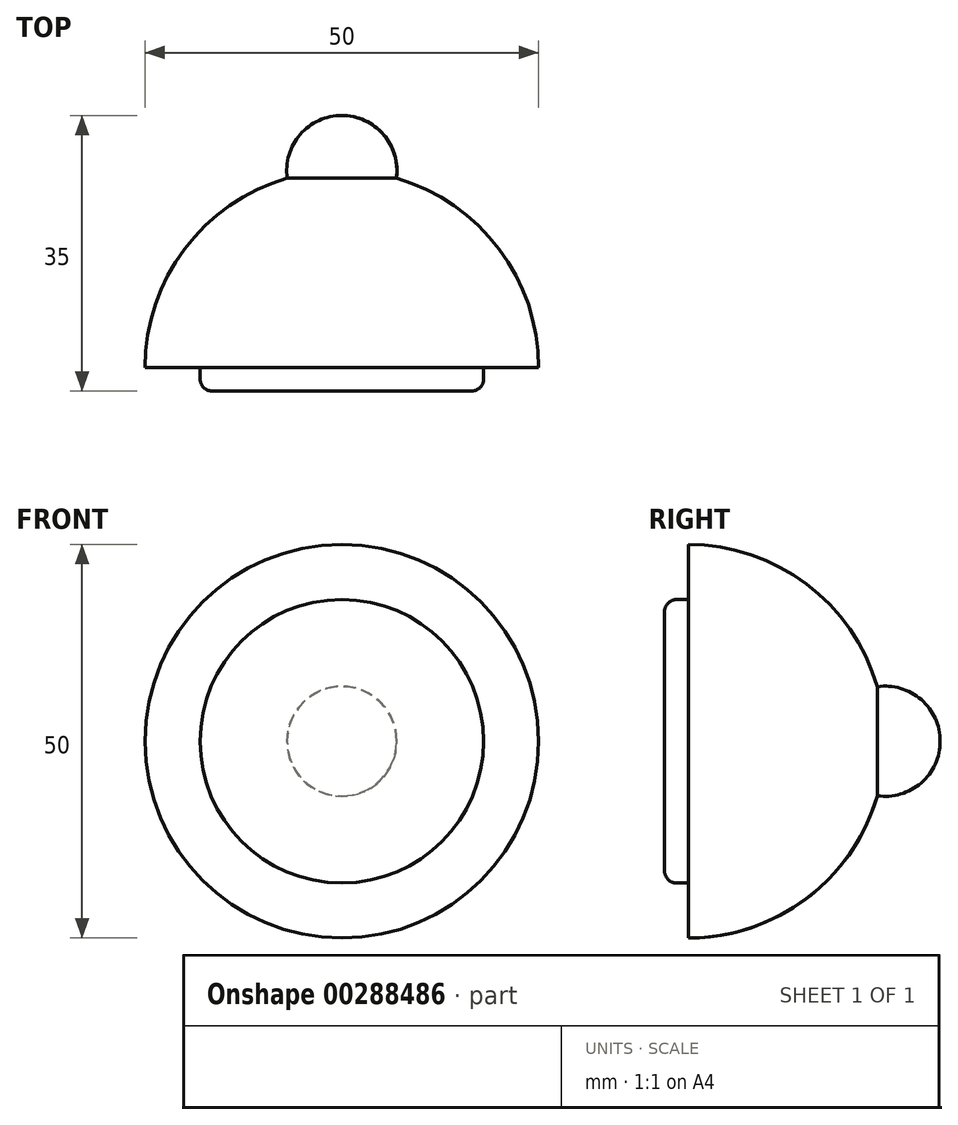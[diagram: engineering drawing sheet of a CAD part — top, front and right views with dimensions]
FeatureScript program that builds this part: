
annotation { "Feature Type Name" : "Feature", "Feature Type Description" : "" }
export const myFeature = defineFeature(function(context is Context, id is Id, definition is map)
    precondition{}
    {
        {
            var Q0;
            Q0=qCreatedBy(makeId("Top.planeOp"),FACE);
            var sketch = newSketch(context, id + "F0", { "sketchPlane" : qUnion([Q0])});
            skPoint(sketch, "E0", {"position": v(0, 25) * mm});
            skPoint(sketch, "E1", {"position": v(25, 0) * mm});
            skArc(sketch, "E2", {"start": v(25, 0) * mm, "mid": v(19.98, 15.03) * mm, "end": v(6.93, 24.02) * mm});
            skLineSegment(sketch, "E3", {"start": v(0, 18) * mm, "end": v(0, 0) * mm});
            skLineSegment(sketch, "E4", {"start": v(25, 0) * mm, "end": v(0, 0) * mm});
            skArc(sketch, "E5", {"start": v(6.93, 24.02) * mm, "mid": v(5.28, 29.6) * mm, "end": v(0, 32) * mm});
            skLineSegment(sketch, "E6", {"start": v(0, 18) * mm, "end": v(0, 32) * mm});
            skSolve(sketch);
        }
        {
            var Q0;
            Q0=makeQuery(id+"F0.imprint","IMPRINT",FACE,{"disambiguationData":[TD([[makeQuery(id+"F0.imprint","IMPRINT",EDGE,{"derivedFrom":sQuery(id+"F0.wireOp",EDGE,"E2")}),1.0]])]});
            var Q1;
            Q1=sQuery(id+"F0.wireOp",EDGE,"E6");
            revolve(context, id + "F1", {"entities" : qUnion([Q0]), "axis" : qUnion([Q1]), "revolveType" : RevolveType.FULL});
        }
        {
            var Q0;
            Q0=qCreatedBy(makeId("Front.planeOp"),FACE);
            var sketch = newSketch(context, id + "F2", { "sketchPlane" : qUnion([Q0])});
            skCircle(sketch, "E7", {"center": v(0, 0) * mm, "radius": 18 * mm});
            skSolve(sketch);
        }
        {
            var Q0;
            Q0=qSketchRegion(id+"F2",true);
            extrude(context, id + "F3", {"entities" : qUnion([Q0]), "operationType" : NewBodyOperationType.ADD, "depth" : 3 * mm});
        }
        {
            var Q0;
            Q0=makeQuery(id+"F3.opExtrude","CAP_EDGE",EDGE,{"disambiguationData":[OSD([sQuery(id+"F2.wireOp",EDGE,"E7")])],"isStart":false});
            fillet(context, id + "F4", {"entities" : qUnion([Q0]), "radius" : 1.5 * mm, "tangentPropagation" : true, "allowEdgeOverflow" : false});
        }
    });
